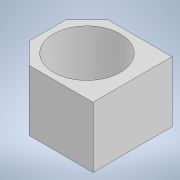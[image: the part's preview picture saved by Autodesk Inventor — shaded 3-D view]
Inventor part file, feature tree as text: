
AUTODESK INVENTOR PART (.ipt)
format: ipt  version: 2022 (Build 260153000, 153)  size: 102,912 bytes
history: native  units: mm
features: extrude x1, sketch x1
ambient origin geometry x8: Origin, YZ Plane, XZ Plane, XY Plane, X Axis, Y Axis, Z Axis, Center Point
bodies: Solid1 (feature_tree)
feature tree (2):
  extrude  "Extrusion1"  Depth=140.0mm
  sketch  "Sketch1"  dims[d0=130.0mm d1=35.0mm d2=35.0mm d3=35.0mm d4=35.0mm d5=65.0mm d6=110.0mm d7=65.0mm d8=100.0mm d9=0.0mm d10=140.0mm]
